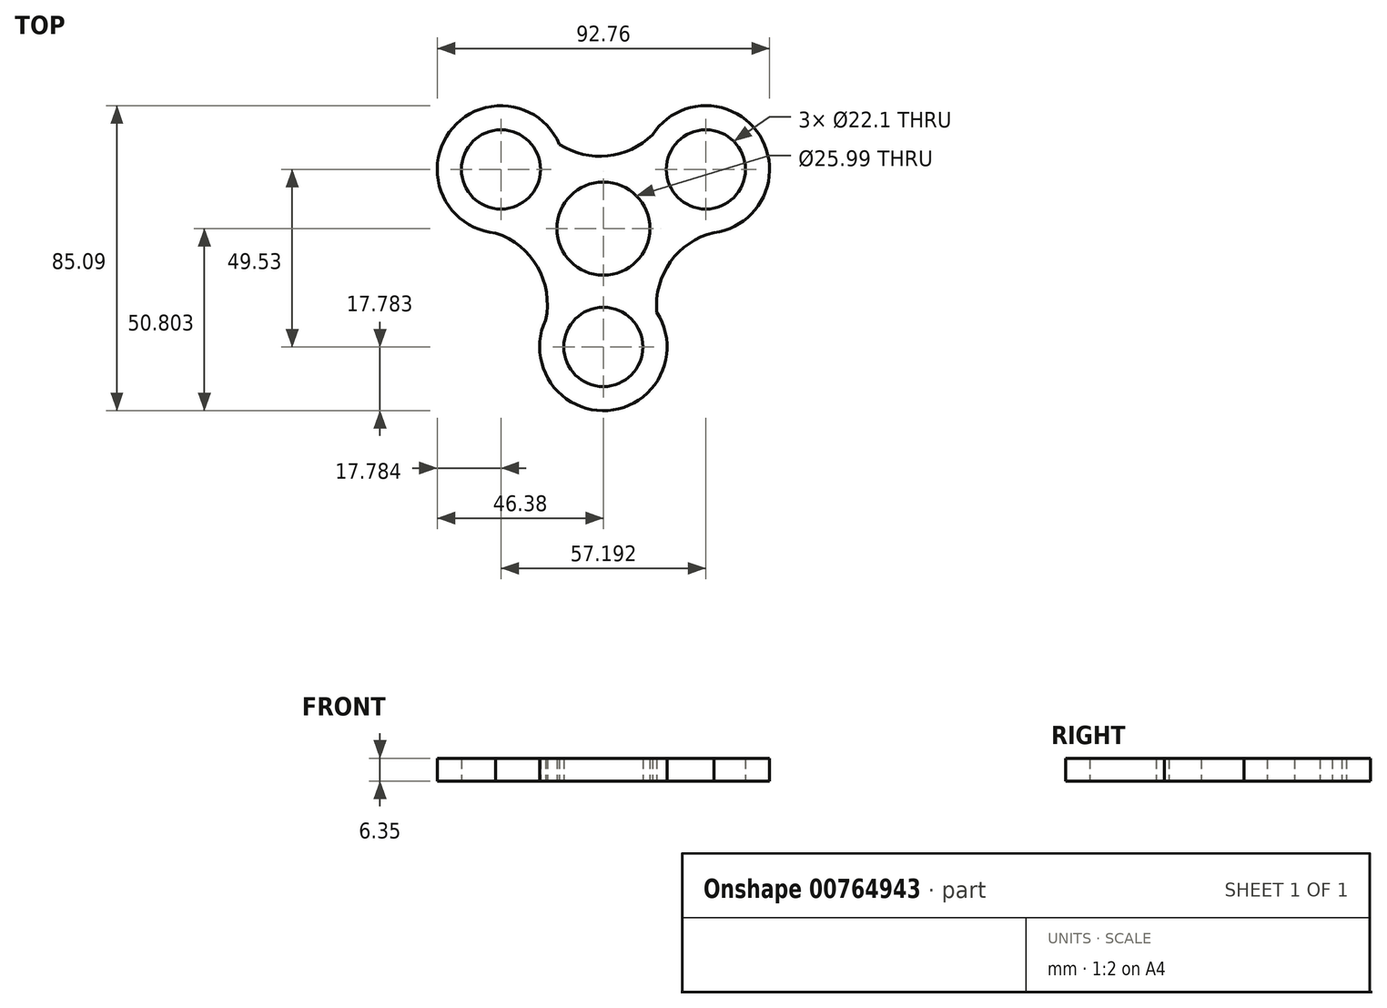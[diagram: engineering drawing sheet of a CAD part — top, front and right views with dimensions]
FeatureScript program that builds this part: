
annotation { "Feature Type Name" : "Feature", "Feature Type Description" : "" }
export const myFeature = defineFeature(function(context is Context, id is Id, definition is map)
    precondition{}
    {
        {
            var Q0;
            Q0=qCreatedBy(makeId("Top.planeOp"),FACE);
            var sketch = newSketch(context, id + "F0", { "sketchPlane" : qUnion([Q0])});
            skCircle(sketch, "E0", {"center": v(0, 13.12) * mm, "radius": 13 * mm});
            skLineSegment(sketch, "E1", {"start": v(0, 13.12) * mm, "end": v(-28.6, 29.63) * mm});
            skLineSegment(sketch, "E2", {"start": v(0, 13.12) * mm, "end": v(28.6, 29.63) * mm});
            skLineSegment(sketch, "E3", {"start": v(0, 13.12) * mm, "end": v(0, -19.9) * mm});
            skCircle(sketch, "E4", {"center": v(-28.6, 29.63) * mm, "radius": 11.05 * mm});
            skCircle(sketch, "E5", {"center": v(28.6, 29.63) * mm, "radius": 11.05 * mm});
            skCircle(sketch, "E6", {"center": v(0, -19.9) * mm, "radius": 11.05 * mm});
            skCircle(sketch, "E7", {"center": v(0, -19.9) * mm, "radius": 17.78 * mm});
            skCircle(sketch, "E8", {"center": v(28.6, 29.63) * mm, "radius": 17.78 * mm});
            skCircle(sketch, "E9", {"center": v(-28.6, 29.63) * mm, "radius": 17.78 * mm});
            skCircle(sketch, "E10", {"center": v(0, 13.12) * mm, "radius": 15.24 * mm});
            skArc(sketch, "E11", {"start": v(-12.26, 36.64) * mm, "mid": v(1.18, 33.41) * mm, "end": v(13.68, 39.3) * mm});
            skArc(sketch, "E12", {"start": v(30.88, 12) * mm, "mid": v(18.74, 3.87) * mm, "end": v(14.93, -10.24) * mm});
            skArc(sketch, "E13", {"start": v(-16.13, -12.42) * mm, "mid": v(-18.4, 2.45) * mm, "end": v(-30.08, 11.92) * mm});
            skSolve(sketch);
        }
        {
            var Q0;
            Q0=makeQuery(id+"F0.imprint","IMPRINT",FACE,{"disambiguationData":[TD([[makeQuery(id+"F0.imprint","IMPRINT",EDGE,{"derivedFrom":sQuery(id+"F0.wireOp",EDGE,"E4")}),-1.0]])]});
            var Q1;
            Q1=makeQuery(id+"F0.imprint","IMPRINT",FACE,{"disambiguationData":[TD([[makeQuery(id+"F0.imprint","IMPRINT",EDGE,{"derivedFrom":sQuery(id+"F0.wireOp",EDGE,"E5")}),-1.0]])]});
            var Q2;
            Q2=makeQuery(id+"F0.imprint","IMPRINT",FACE,{"disambiguationData":[TD([[makeQuery(id+"F0.imprint","IMPRINT",EDGE,{"derivedFrom":sQuery(id+"F0.wireOp",EDGE,"E6")}),-1.0]])]});
            var Q3;
            {var subQ0=sQuery(id+"F0.wireOp",EDGE,"E12");Q3=makeQuery(id+"F0.imprint","IMPRINT",FACE,{"disambiguationData":[TD([[makeQuery(id+"F0.imprint","IMPRINT",EDGE,{"derivedFrom":subQ0}),-1.0]])]});}
            var Q4;
            {var subQ0=sQuery(id+"F0.wireOp",EDGE,"E11");Q4=makeQuery(id+"F0.imprint","IMPRINT",FACE,{"disambiguationData":[TD([[makeQuery(id+"F0.imprint","IMPRINT",EDGE,{"derivedFrom":subQ0}),-1.0]])]});}
            var Q5;
            {var subQ0=sQuery(id+"F0.wireOp",EDGE,"E13");Q5=makeQuery(id+"F0.imprint","IMPRINT",FACE,{"disambiguationData":[TD([[makeQuery(id+"F0.imprint","IMPRINT",EDGE,{"derivedFrom":subQ0}),-1.0]])]});}
            var Q6;
            {var subQ0=sQuery(id+"F0.wireOp",EDGE,"E1");var subQ1=sQuery(id+"F0.wireOp",EDGE,"E0");var subQ2=makeQuery(id+"F0.imprint","INTERSECT",VERTEX,{"derivedFrom":[subQ1,subQ0]});Q6=makeQuery(id+"F0.imprint","IMPRINT",FACE,{"disambiguationData":[TD([[makeQuery(id+"F0.imprint","IMPRINT",EDGE,{"disambiguationData":[TD([[subQ2,-1.0]])],"derivedFrom":subQ1}),-1.0]])]});}
            var Q7;
            {var subQ0=sQuery(id+"F0.wireOp",EDGE,"E1");var subQ1=sQuery(id+"F0.wireOp",EDGE,"E0");var subQ2=makeQuery(id+"F0.imprint","INTERSECT",VERTEX,{"derivedFrom":[subQ1,subQ0]});Q7=makeQuery(id+"F0.imprint","IMPRINT",FACE,{"disambiguationData":[TD([[makeQuery(id+"F0.imprint","IMPRINT",EDGE,{"disambiguationData":[TD([[subQ2,1.0]])],"derivedFrom":subQ1}),-1.0]])]});}
            var Q8;
            {var subQ0=sQuery(id+"F0.wireOp",EDGE,"E2");var subQ1=sQuery(id+"F0.wireOp",EDGE,"E0");var subQ2=makeQuery(id+"F0.imprint","INTERSECT",VERTEX,{"derivedFrom":[subQ1,subQ0]});Q8=makeQuery(id+"F0.imprint","IMPRINT",FACE,{"disambiguationData":[TD([[makeQuery(id+"F0.imprint","IMPRINT",EDGE,{"disambiguationData":[TD([[subQ2,1.0]])],"derivedFrom":subQ1}),-1.0]])]});}
            extrude(context, id + "F1", {"entities" : qUnion([Q0, Q1, Q2, Q3, Q4, Q5, Q6, Q7, Q8]), "depth" : 6.35 * mm, "offsetDistance" : 25.4 * mm});
        }
    });
